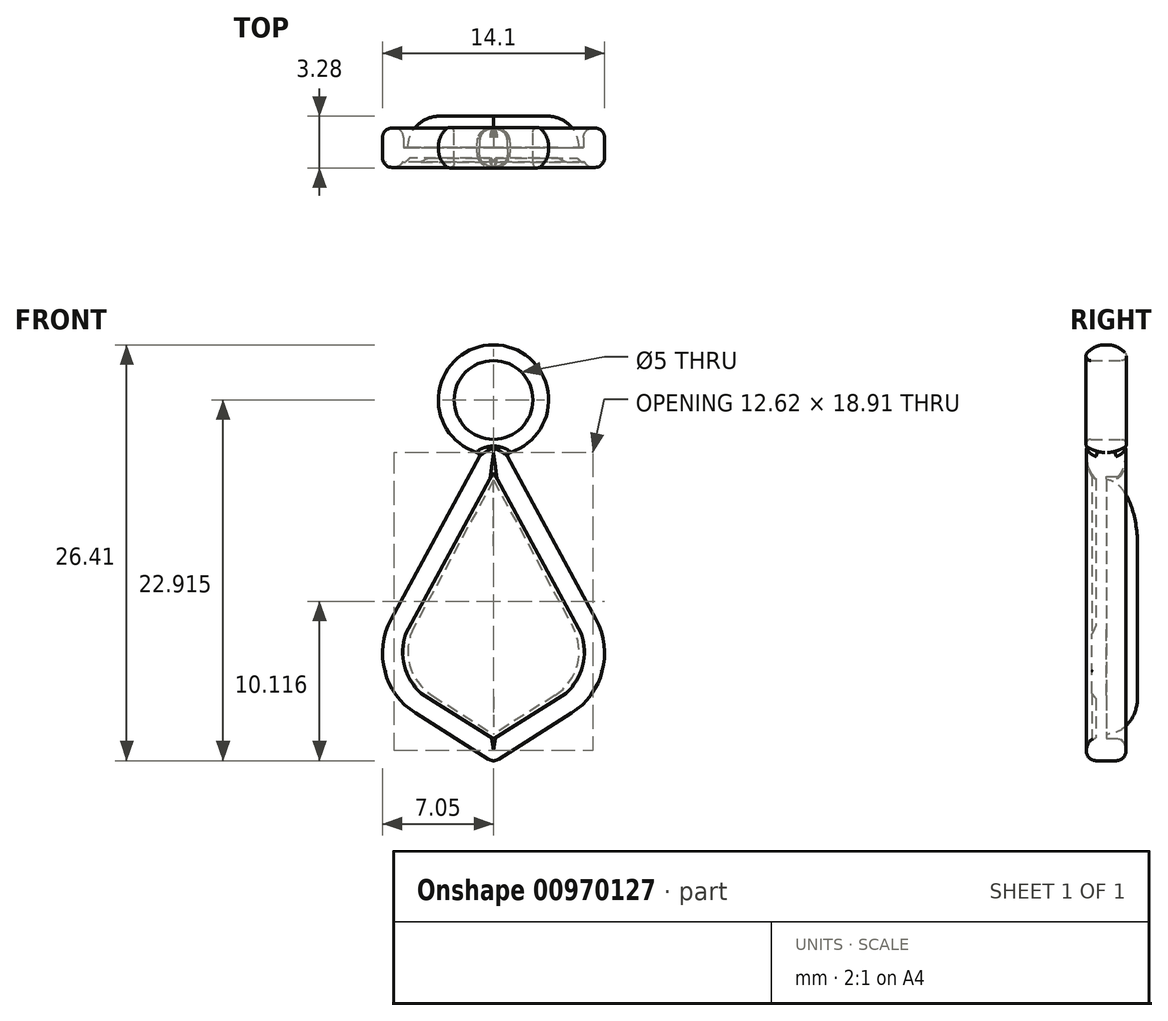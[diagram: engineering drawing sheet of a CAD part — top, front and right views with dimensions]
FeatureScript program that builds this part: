
annotation { "Feature Type Name" : "Feature", "Feature Type Description" : "" }
export const myFeature = defineFeature(function(context is Context, id is Id, definition is map)
    precondition{}
    {
        {
            var Q0;
            Q0=qCreatedBy(makeId("Front.planeOp"),FACE);
            var sketch = newSketch(context, id + "F0", { "sketchPlane" : qUnion([Q0])});
            skCircle(sketch, "E0", {"center": v(0, 12.12) * mm, "radius": 3.5 * mm});
            skCircle(sketch, "E1", {"center": v(0, 12.12) * mm, "radius": 2.5 * mm});
            skSolve(sketch);
        }
        {
            var Q0;
            Q0=makeQuery(id+"F0.imprint","IMPRINT",FACE,{"disambiguationData":[TD([[makeQuery(id+"F0.imprint","IMPRINT",EDGE,{"derivedFrom":sQuery(id+"F0.wireOp",EDGE,"E0")}),1.0]])]});
            extrude(context, id + "F1", {"entities" : qUnion([Q0]), "depth" : 1.5 * mm, "offsetDistance" : 25 * mm, "hasSecondDirection" : true, "secondDirectionOppositeDirection" : true, "secondDirectionDepth" : 1.5 * mm});
        }
        {
            var Q0;
            Q0=makeQuery(id+"F1.opExtrude","CAP_EDGE",EDGE,{"disambiguationData":[OSD([sQuery(id+"F0.wireOp",EDGE,"E0")])],"isStart":true});
            var Q1;
            Q1=makeQuery(id+"F1.opExtrude","CAP_EDGE",EDGE,{"disambiguationData":[OSD([sQuery(id+"F0.wireOp",EDGE,"E0")])],"isStart":false});
            fillet(context, id + "F2", {"entities" : qUnion([Q0, Q1]), "radius" : 1.5 * mm, "tangentPropagation" : true, "allowEdgeOverflow" : false});
        }
        {
            var Q0;
            Q0=makeQuery(id+"F1.opExtrude","SWEPT_FACE",FACE,{"disambiguationData":[OSD([sQuery(id+"F0.wireOp",EDGE,"E1")])]});
            var Q1;
            Q1=makeQuery(id+"F2.opFillet","BLEND_EDGE",EDGE,{"blendedFrom":[makeQuery(id+"F1.opExtrude","CAP_EDGE",EDGE,{"disambiguationData":[OSD([sQuery(id+"F0.wireOp",EDGE,"E0")])],"isStart":true}),makeQuery(id+"F1.opExtrude","SWEPT_FACE",FACE,{"disambiguationData":[OSD([sQuery(id+"F0.wireOp",EDGE,"E1")])]})],"blendedInto":[makeQuery(id+"F1.opExtrude","SWEPT_FACE",FACE,{"disambiguationData":[OSD([sQuery(id+"F0.wireOp",EDGE,"E1")])]})]});
            var Q2;
            Q2=makeQuery(id+"F2.opFillet","BLEND_EDGE",EDGE,{"blendedFrom":[makeQuery(id+"F1.opExtrude","CAP_EDGE",EDGE,{"disambiguationData":[OSD([sQuery(id+"F0.wireOp",EDGE,"E0")])],"isStart":false}),makeQuery(id+"F1.opExtrude","SWEPT_FACE",FACE,{"disambiguationData":[OSD([sQuery(id+"F0.wireOp",EDGE,"E1")])]})],"blendedInto":[makeQuery(id+"F1.opExtrude","SWEPT_FACE",FACE,{"disambiguationData":[OSD([sQuery(id+"F0.wireOp",EDGE,"E1")])]})]});
            fillet(context, id + "F3", {"entities" : qUnion([Q0, Q1, Q2]), "radius" : .3 * mm, "tangentPropagation" : true, "allowEdgeOverflow" : false});
        }
        {
            var Q0;
            Q0=qCreatedBy(makeId("Front.planeOp"),FACE);
            var sketch = newSketch(context, id + "F4", { "sketchPlane" : qUnion([Q0])});
            skLineSegment(sketch, "E2", {"start": v(0, 10.14) * mm, "end": v(8.52, -5.52) * mm});
            skLineSegment(sketch, "E3", {"start": v(8.52, -5.52) * mm, "end": v(0, -10.9) * mm});
            skLineSegment(sketch, "E4.MirrorCS", {"start": v(0, 10.14) * mm, "end": v(-8.52, -5.52) * mm});
            skLineSegment(sketch, "E5.MirrorCS", {"start": v(-8.52, -5.52) * mm, "end": v(0, -10.9) * mm});
            skLineSegment(sketch, "E6.0", {"start": v(0, 7.53) * mm, "end": v(6.86, -5.09) * mm});
            skLineSegment(sketch, "E6.1", {"start": v(0, 7.53) * mm, "end": v(-6.86, -5.09) * mm});
            skLineSegment(sketch, "E6.2", {"start": v(-6.86, -5.09) * mm, "end": v(0, -9.42) * mm});
            skLineSegment(sketch, "E6.3", {"start": v(6.86, -5.09) * mm, "end": v(0, -9.42) * mm});
            skSolve(sketch);
        }
        {
            var Q0;
            Q0=makeQuery(id+"F4.imprint","IMPRINT",FACE,{"disambiguationData":[TD([[makeQuery(id+"F4.imprint","IMPRINT",EDGE,{"derivedFrom":sQuery(id+"F4.wireOp",EDGE,"E2")}),-1.0]])]});
            extrude(context, id + "F5", {"entities" : qUnion([Q0]), "depth" : 1.25 * mm, "offsetDistance" : 25 * mm, "hasSecondDirection" : true, "secondDirectionOppositeDirection" : true, "secondDirectionDepth" : 1.25 * mm});
        }
        {
            var Q0;
            Q0=makeQuery(id+"F5.opExtrude","SWEPT_EDGE",EDGE,{"disambiguationData":[OSD([sQuery(id+"F4.wireOp",EDGE,"E4.MirrorCS"),sQuery(id+"F4.wireOp",EDGE,"E5.MirrorCS")])]});
            var Q1;
            Q1=makeQuery(id+"F5.opExtrude","SWEPT_EDGE",EDGE,{"disambiguationData":[OSD([sQuery(id+"F4.wireOp",EDGE,"E2"),sQuery(id+"F4.wireOp",EDGE,"E3")])]});
            fillet(context, id + "F6", {"entities" : qUnion([Q0, Q1]), "radius" : 4.5 * mm, "tangentPropagation" : true, "allowEdgeOverflow" : false});
        }
        {
            var Q0;
            Q0=makeQuery(id+"F5.opExtrude","SWEPT_EDGE",EDGE,{"disambiguationData":[OSD([sQuery(id+"F4.wireOp",EDGE,"E6.0"),sQuery(id+"F4.wireOp",EDGE,"E6.3")])]});
            var Q1;
            Q1=makeQuery(id+"F5.opExtrude","SWEPT_EDGE",EDGE,{"disambiguationData":[OSD([sQuery(id+"F4.wireOp",EDGE,"E6.1"),sQuery(id+"F4.wireOp",EDGE,"E6.2")])]});
            fillet(context, id + "F7", {"entities" : qUnion([Q0, Q1]), "radius" : 3.5 * mm, "tangentPropagation" : true, "allowEdgeOverflow" : false});
        }
        {
            var Q0;
            {var subQ0=sQuery(id+"F4.wireOp",EDGE,"E3");var subQ1=sQuery(id+"F4.wireOp",EDGE,"E2");Q0=makeQuery(id+"F6.opFillet","BLEND_EDGE",EDGE,{"blendedFrom":[makeQuery(id+"F5.opExtrude","SWEPT_EDGE",EDGE,{"disambiguationData":[OSD([subQ1,subQ0])]}),makeQuery(id+"F5.opExtrude","CAP_FACE",FACE,{"disambiguationData":[OSD([subQ1,subQ0,sQuery(id+"F4.wireOp",EDGE,"E4.MirrorCS"),sQuery(id+"F4.wireOp",EDGE,"E5.MirrorCS"),sQuery(id+"F4.wireOp",EDGE,"E6.0"),sQuery(id+"F4.wireOp",EDGE,"E6.1"),sQuery(id+"F4.wireOp",EDGE,"E6.2"),sQuery(id+"F4.wireOp",EDGE,"E6.3")])],"isStart":false})],"blendedInto":[makeQuery(id+"F5.opExtrude","CAP_FACE",FACE,{"disambiguationData":[OSD([subQ1,subQ0,sQuery(id+"F4.wireOp",EDGE,"E4.MirrorCS"),sQuery(id+"F4.wireOp",EDGE,"E5.MirrorCS"),sQuery(id+"F4.wireOp",EDGE,"E6.0"),sQuery(id+"F4.wireOp",EDGE,"E6.1"),sQuery(id+"F4.wireOp",EDGE,"E6.2"),sQuery(id+"F4.wireOp",EDGE,"E6.3")])],"isStart":false})]});}
            var Q1;
            Q1=makeQuery(id+"F5.opExtrude","CAP_EDGE",EDGE,{"disambiguationData":[OSD([sQuery(id+"F4.wireOp",EDGE,"E3")])],"isStart":false});
            var Q2;
            Q2=makeQuery(id+"F5.opExtrude","CAP_EDGE",EDGE,{"disambiguationData":[OSD([sQuery(id+"F4.wireOp",EDGE,"E6.0")])],"isStart":false});
            var Q3;
            Q3=makeQuery(id+"F5.opExtrude","CAP_EDGE",EDGE,{"disambiguationData":[OSD([sQuery(id+"F4.wireOp",EDGE,"E5.MirrorCS")])],"isStart":false});
            var Q4;
            Q4=makeQuery(id+"F5.opExtrude","CAP_EDGE",EDGE,{"disambiguationData":[OSD([sQuery(id+"F4.wireOp",EDGE,"E6.2")])],"isStart":false});
            var Q5;
            {var subQ0=sQuery(id+"F4.wireOp",EDGE,"E5.MirrorCS");var subQ1=sQuery(id+"F4.wireOp",EDGE,"E4.MirrorCS");Q5=makeQuery(id+"F6.opFillet","BLEND_EDGE",EDGE,{"blendedFrom":[makeQuery(id+"F5.opExtrude","SWEPT_EDGE",EDGE,{"disambiguationData":[OSD([subQ1,subQ0])]}),makeQuery(id+"F5.opExtrude","CAP_FACE",FACE,{"disambiguationData":[OSD([sQuery(id+"F4.wireOp",EDGE,"E2"),sQuery(id+"F4.wireOp",EDGE,"E3"),subQ1,subQ0,sQuery(id+"F4.wireOp",EDGE,"E6.0"),sQuery(id+"F4.wireOp",EDGE,"E6.1"),sQuery(id+"F4.wireOp",EDGE,"E6.2"),sQuery(id+"F4.wireOp",EDGE,"E6.3")])],"isStart":true})],"blendedInto":[makeQuery(id+"F5.opExtrude","CAP_FACE",FACE,{"disambiguationData":[OSD([sQuery(id+"F4.wireOp",EDGE,"E2"),sQuery(id+"F4.wireOp",EDGE,"E3"),subQ1,subQ0,sQuery(id+"F4.wireOp",EDGE,"E6.0"),sQuery(id+"F4.wireOp",EDGE,"E6.1"),sQuery(id+"F4.wireOp",EDGE,"E6.2"),sQuery(id+"F4.wireOp",EDGE,"E6.3")])],"isStart":true})]});}
            var Q6;
            Q6=makeQuery(id+"F5.opExtrude","CAP_EDGE",EDGE,{"disambiguationData":[OSD([sQuery(id+"F4.wireOp",EDGE,"E6.1")])],"isStart":true});
            var Q7;
            Q7=makeQuery(id+"F5.opExtrude","CAP_EDGE",EDGE,{"disambiguationData":[OSD([sQuery(id+"F4.wireOp",EDGE,"E6.0")])],"isStart":true});
            var Q8;
            Q8=makeQuery(id+"F5.opExtrude","CAP_EDGE",EDGE,{"disambiguationData":[OSD([sQuery(id+"F4.wireOp",EDGE,"E3")])],"isStart":true});
            var Q9;
            Q9=makeQuery(id+"F5.opExtrude","SWEPT_EDGE",EDGE,{"disambiguationData":[OSD([sQuery(id+"F4.wireOp",EDGE,"E3"),sQuery(id+"F4.wireOp",EDGE,"E5.MirrorCS")])]});
            fillet(context, id + "F8", {"entities" : qUnion([Q0, Q1, Q2, Q3, Q4, Q5, Q6, Q7, Q8, Q9]), "radius" : .6 * mm, "tangentPropagation" : true, "allowEdgeOverflow" : false});
        }
        {
            var Q0;
            Q0=makeQuery(id+"F8.opFillet","BLEND_EDGE",EDGE,{"blendedFrom":[makeQuery(id+"F5.opExtrude","CAP_EDGE",EDGE,{"disambiguationData":[OSD([sQuery(id+"F4.wireOp",EDGE,"E6.0")])],"isStart":false}),makeQuery(id+"F5.opExtrude","CAP_EDGE",EDGE,{"disambiguationData":[OSD([sQuery(id+"F4.wireOp",EDGE,"E6.1")])],"isStart":false})],"blendedInto":[]});
            var Q1;
            Q1=makeQuery(id+"F5.opExtrude","SWEPT_EDGE",EDGE,{"disambiguationData":[OSD([sQuery(id+"F4.wireOp",EDGE,"E6.2"),sQuery(id+"F4.wireOp",EDGE,"E6.3")])]});
            fillet(context, id + "F9", {"entities" : qUnion([Q0, Q1]), "radius" : .25 * mm, "tangentPropagation" : true, "allowEdgeOverflow" : false});
        }
        {
            var Q0;
            Q0=makeQuery(id+"F5.opExtrude","SWEPT_EDGE",EDGE,{"disambiguationData":[OSD([sQuery(id+"F4.wireOp",EDGE,"E2"),sQuery(id+"F4.wireOp",EDGE,"E4.MirrorCS")])]});
            fillet(context, id + "F10", {"entities" : qUnion([Q0]), "radius" : .5 * mm, "tangentPropagation" : true, "allowEdgeOverflow" : false});
        }
        {
            var Q0;
            Q0=makeQuery(id+"F4.imprint","IMPRINT",FACE,{"disambiguationData":[TD([[makeQuery(id+"F4.imprint","IMPRINT",EDGE,{"derivedFrom":sQuery(id+"F4.wireOp",EDGE,"E6.0")}),-1.0]])]});
            extrude(context, id + "F11", {"entities" : qUnion([Q0]), "depth" : .9 * mm, "offsetDistance" : 25 * mm});
        }
        {
            var Q0;
            Q0=qCreatedBy(makeId("Front.planeOp"),FACE);
            var sketch = newSketch(context, id + "F12", { "sketchPlane" : qUnion([Q0])});
            skLineSegment(sketch, "E7", {"start": v(0, 7.05) * mm, "end": v(-6.5, -5) * mm});
            skLineSegment(sketch, "E8", {"start": v(-6.5, -5) * mm, "end": v(0, -9.1) * mm});
            skLineSegment(sketch, "E9.MirrorCS", {"start": v(6.5, -5) * mm, "end": v(0, -9.1) * mm});
            skLineSegment(sketch, "E10.MirrorCS", {"start": v(0, 7.05) * mm, "end": v(6.5, -5) * mm});
            skSolve(sketch);
        }
        {
            var Q0;
            Q0 = qSketchRegion(id + "F12", true);
            extrude(context, id + "F13", {"entities" : qUnion([Q0]), "oppositeDirection" : true, "depth" : 2 * mm, "offsetDistance" : 25 * mm});
        }
        {
            var Q0;
            Q0=makeQuery(id+"F13.opExtrude","SWEPT_EDGE",EDGE,{"disambiguationData":[OSD([sQuery(id+"F12.wireOp",EDGE,"E7"),sQuery(id+"F12.wireOp",EDGE,"E8")])]});
            var Q1;
            Q1=makeQuery(id+"F13.opExtrude","SWEPT_EDGE",EDGE,{"disambiguationData":[OSD([sQuery(id+"F12.wireOp",EDGE,"E9.MirrorCS"),sQuery(id+"F12.wireOp",EDGE,"E10.MirrorCS")])]});
            fillet(context, id + "F14", {"entities" : qUnion([Q0, Q1]), "radius" : 3.3 * mm, "tangentPropagation" : true, "allowEdgeOverflow" : false});
        }
        {
            var Q0;
            Q0=makeQuery(id+"F13.opExtrude","CAP_FACE",FACE,{"disambiguationData":[OSD([sQuery(id+"F12.wireOp",EDGE,"E7"),sQuery(id+"F12.wireOp",EDGE,"E8"),sQuery(id+"F12.wireOp",EDGE,"E9.MirrorCS"),sQuery(id+"F12.wireOp",EDGE,"E10.MirrorCS")])],"isStart":false});
            fillet(context, id + "F15", {"entities" : qUnion([Q0]), "radius" : 2 * mm, "tangentPropagation" : true, "allowEdgeOverflow" : false});
        }
        {
            var Q0;
            Q0=makeQuery(id+"F11.opExtrude","SWEPT_BODY",BODY,{"disambiguationData":[OSD([sQuery(id+"F4.wireOp",EDGE,"E6.0"),sQuery(id+"F4.wireOp",EDGE,"E6.1"),sQuery(id+"F4.wireOp",EDGE,"E6.2"),sQuery(id+"F4.wireOp",EDGE,"E6.3")])]});
            var Q1;
            Q1=makeQuery(id+"F1.opExtrude","SWEPT_BODY",BODY,{"disambiguationData":[OSD([sQuery(id+"F0.wireOp",EDGE,"E0"),sQuery(id+"F0.wireOp",EDGE,"E1")])]});
            var Q2;
            Q2=makeQuery(id+"F5.opExtrude","SWEPT_BODY",BODY,{"disambiguationData":[OSD([sQuery(id+"F4.wireOp",EDGE,"E2"),sQuery(id+"F4.wireOp",EDGE,"E3"),sQuery(id+"F4.wireOp",EDGE,"E4.MirrorCS"),sQuery(id+"F4.wireOp",EDGE,"E5.MirrorCS"),sQuery(id+"F4.wireOp",EDGE,"E6.0"),sQuery(id+"F4.wireOp",EDGE,"E6.1"),sQuery(id+"F4.wireOp",EDGE,"E6.2"),sQuery(id+"F4.wireOp",EDGE,"E6.3")])]});
            booleanBodies(context, id + "F16", {"operationType" : BooleanOperationType.UNION, "tools" : qUnion([Q0, Q1, Q2])});
        }
        {
            var Q0;
            {var subQ0=sQuery(id+"F0.wireOp",EDGE,"E0");Q0=makeQuery(id+"F16.opBoolean","INTERSECT",EDGE,{"derivedFrom":[makeQuery(id+"F2.opFillet","BLEND_FACE",FACE,{"disambiguationData":[OSD([subQ0]),TDD([makeQuery(id+"F1.opExtrude","CAP_EDGE",EDGE,{"disambiguationData":[OSD([subQ0])],"isStart":false})])]}),makeQuery(id+"F5.opExtrude","SWEPT_FACE",FACE,{"disambiguationData":[OSD([sQuery(id+"F4.wireOp",EDGE,"E2")])]})]});}
            fillet(context, id + "F17", {"entities" : qUnion([Q0]), "radius" : .25 * mm, "tangentPropagation" : true, "allowEdgeOverflow" : false});
        }
    });
